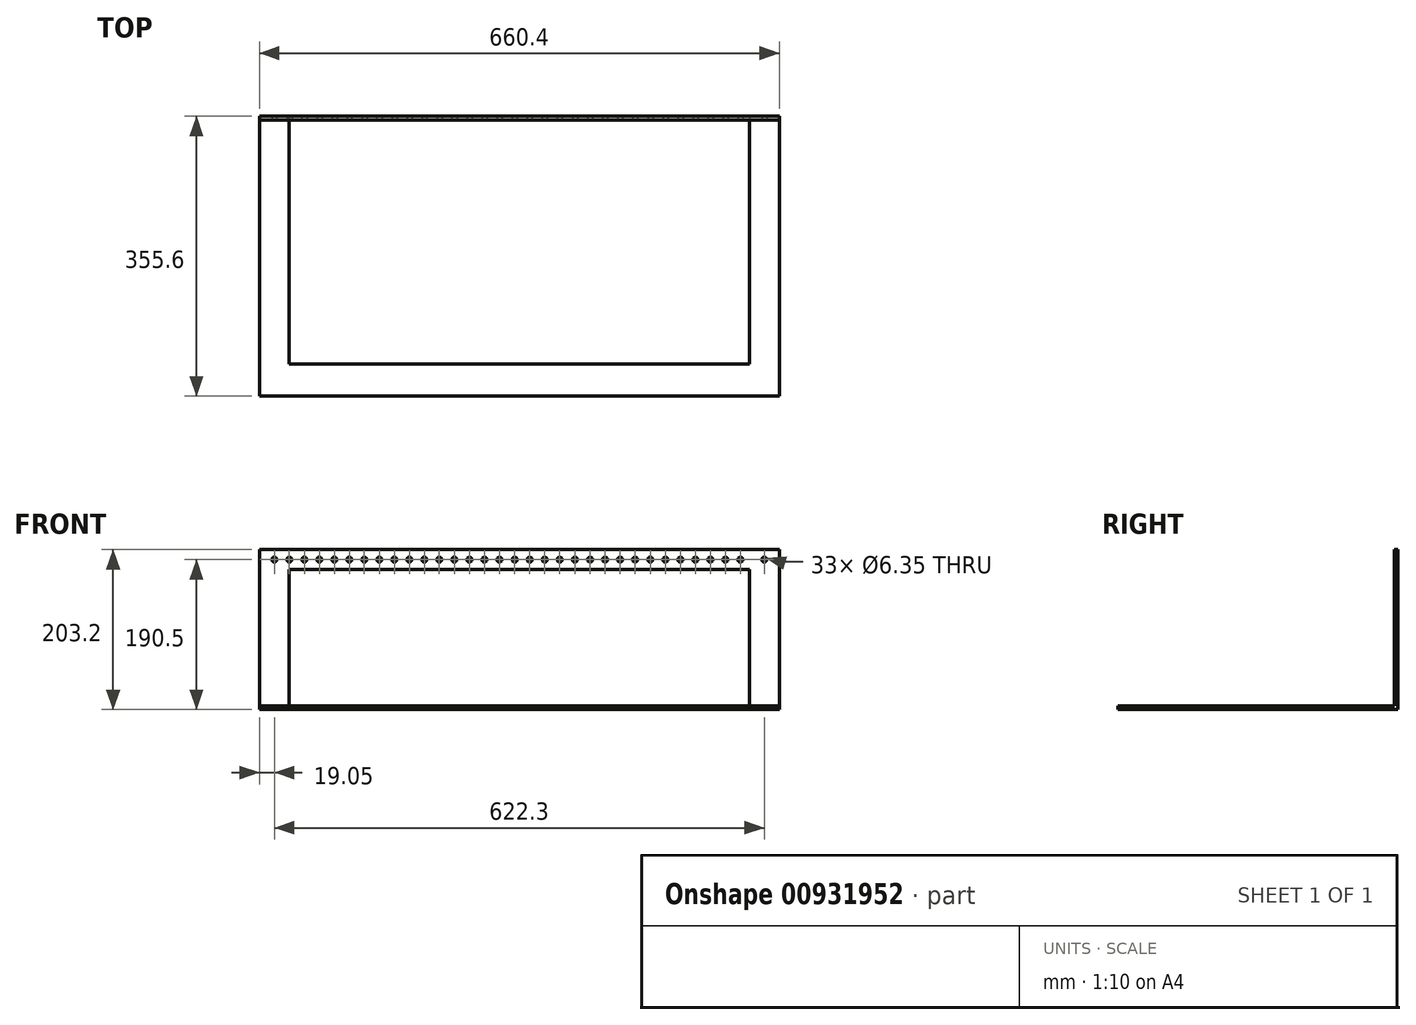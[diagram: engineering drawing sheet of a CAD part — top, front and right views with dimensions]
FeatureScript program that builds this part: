
annotation { "Feature Type Name" : "Feature", "Feature Type Description" : "" }
export const myFeature = defineFeature(function(context is Context, id is Id, definition is map)
    precondition{}
    {
        {
            var Q0;
            Q0=qCreatedBy(makeId("Right.planeOp"),FACE);
            var sketch = newSketch(context, id + "F0", { "sketchPlane" : qUnion([Q0])});
            skLineSegment(sketch, "E0", {"start": v(-188.84, 0) * mm, "end": v(166.76, 0) * mm});
            skLineSegment(sketch, "E1", {"start": v(166.76, 0) * mm, "end": v(166.76, 203.2) * mm});
            skLineSegment(sketch, "E2", {"start": v(-188.84, 0) * mm, "end": v(-188.84, 4.78) * mm});
            skLineSegment(sketch, "E3", {"start": v(-188.84, 4.78) * mm, "end": v(161.98, 4.78) * mm});
            skLineSegment(sketch, "E4", {"start": v(161.98, 4.78) * mm, "end": v(161.98, 203.2) * mm});
            skLineSegment(sketch, "E5", {"start": v(161.98, 203.2) * mm, "end": v(166.76, 203.2) * mm});
            skSolve(sketch);
        }
        {
            var Q0;
            Q0=makeQuery(id+"F0.imprint","IMPRINT",FACE,{"disambiguationData":[TD([[makeQuery(id+"F0.imprint","IMPRINT",EDGE,{"derivedFrom":sQuery(id+"F0.wireOp",EDGE,"E0")}),1.0]])]});
            extrude(context, id + "F1", {"entities" : qUnion([Q0]), "depth" : 660.4 * mm, "offsetDistance" : 25.4 * mm});
        }
        {
            var Q0;
            Q0=makeQuery(id+"F1.opExtrude","SWEPT_FACE",FACE,{"disambiguationData":[OSD([sQuery(id+"F0.wireOp",EDGE,"E2")])]});
            var sketch = newSketch(context, id + "F2", { "sketchPlane" : qUnion([Q0])});
            skLineSegment(sketch, "E6", {"start": v(38.1, 4.78) * mm, "end": v(38.1, 177.8) * mm});
            skLineSegment(sketch, "E7", {"start": v(38.1, 177.8) * mm, "end": v(622.3, 177.8) * mm});
            skLineSegment(sketch, "E8", {"start": v(622.3, 177.8) * mm, "end": v(622.3, 4.78) * mm});
            skLineSegment(sketch, "E9", {"start": v(622.3, 4.78) * mm, "end": v(38.1, 4.78) * mm});
            skSolve(sketch);
        }
        {
            var Q0;
            Q0=makeQuery(id+"F2.imprint","IMPRINT",FACE,{"disambiguationData":[TD([[makeQuery(id+"F2.imprint","IMPRINT",EDGE,{"derivedFrom":sQuery(id+"F2.wireOp",EDGE,"E6")}),-1.0]])]});
            extrude(context, id + "F3", {"entities" : qUnion([Q0]), "operationType" : NewBodyOperationType.REMOVE, "endBound" : BoundingType.THROUGH_ALL, "oppositeDirection" : true, "depth" : 254 * mm, "offsetDistance" : 25.4 * mm});
        }
        {
            var Q0;
            Q0=makeQuery(id+"F3.boolean.opBoolean","MERGE",FACE,{"derivedFrom":[makeQuery(id+"F1.opExtrude","SWEPT_FACE",FACE,{"disambiguationData":[OSD([sQuery(id+"F0.wireOp",EDGE,"E3")])]})],"fromTools":[makeQuery(id+"F3.opExtrude","SWEPT_FACE",FACE,{"disambiguationData":[OSD([sQuery(id+"F2.wireOp",EDGE,"E9")])]})]});
            var sketch = newSketch(context, id + "F4", { "sketchPlane" : qUnion([Q0])});
            skLineSegment(sketch, "E10", {"start": v(38.1, 166.76) * mm, "end": v(38.1, -148.16) * mm});
            skLineSegment(sketch, "E11", {"start": v(38.1, -148.16) * mm, "end": v(622.3, -148.16) * mm});
            skLineSegment(sketch, "E12", {"start": v(622.3, -148.16) * mm, "end": v(622.3, 166.76) * mm});
            skLineSegment(sketch, "E13", {"start": v(622.3, 166.76) * mm, "end": v(38.1, 166.76) * mm});
            skLineSegment(sketch, "E14", {"start": v(38.1, 161.98) * mm, "end": v(38.1, 166.76) * mm});
            skSolve(sketch);
        }
        {
            var Q0;
            Q0 = qSketchRegion(id + "F4", true);
            extrude(context, id + "F5", {"entities" : qUnion([Q0]), "operationType" : NewBodyOperationType.REMOVE, "oppositeDirection" : true, "depth" : 25.4 * mm, "offsetDistance" : 25.4 * mm});
        }
        {
            var Q0;
            Q0=makeQuery(id+"F1.opExtrude","SWEPT_FACE",FACE,{"disambiguationData":[OSD([sQuery(id+"F0.wireOp",EDGE,"E4")])]});
            var sketch = newSketch(context, id + "F6", { "sketchPlane" : qUnion([Q0])});
            skLineSegment(sketch, "E15", {"start": v(0, 190.5) * mm, "end": v(114.3, 190.5) * mm, "construction": true});
            skLineSegment(sketch, "E16", {"start": v(114.3, 190.5) * mm, "end": v(660.4, 190.5) * mm, "construction": true});
            skPoint(sketch, "E17", {"position": v(19.05, 190.5) * mm});
            skPoint(sketch, "E18", {"position": v(38.1, 190.5) * mm});
            skPoint(sketch, "E19", {"position": v(57.15, 190.5) * mm});
            skPoint(sketch, "E20", {"position": v(76.2, 190.5) * mm});
            skPoint(sketch, "E21", {"position": v(95.25, 190.5) * mm});
            skPoint(sketch, "E22", {"position": v(114.3, 190.5) * mm});
            skPoint(sketch, "E23", {"position": v(133.35, 190.5) * mm});
            skPoint(sketch, "E24", {"position": v(152.4, 190.5) * mm});
            skPoint(sketch, "E25", {"position": v(171.45, 190.5) * mm});
            skPoint(sketch, "E26", {"position": v(190.5, 190.5) * mm});
            skPoint(sketch, "E27", {"position": v(209.55, 190.5) * mm});
            skPoint(sketch, "E28", {"position": v(228.6, 190.5) * mm});
            skPoint(sketch, "E29", {"position": v(247.65, 190.5) * mm});
            skPoint(sketch, "E30.1.0.0", {"position": v(305.05, 190.5) * mm});
            skPoint(sketch, "E30.1.0.1", {"position": v(286, 190.5) * mm});
            skPoint(sketch, "E30.1.0.2", {"position": v(266.95, 190.5) * mm});
            skPoint(sketch, "E30.1.0.3", {"position": v(247.9, 190.5) * mm});
            skLineSegment(sketch, "E30.1.0.4", {"start": v(190.75, 190.5) * mm, "end": v(736.85, 190.5) * mm, "construction": true});
            skPoint(sketch, "E30.2.0.0", {"position": v(381.5, 190.5) * mm});
            skPoint(sketch, "E30.2.0.1", {"position": v(362.46, 190.5) * mm});
            skPoint(sketch, "E30.2.0.2", {"position": v(343.4, 190.5) * mm});
            skPoint(sketch, "E30.2.0.3", {"position": v(324.36, 190.5) * mm});
            skLineSegment(sketch, "E30.2.0.4", {"start": v(267.2, 190.5) * mm, "end": v(813.3, 190.5) * mm, "construction": true});
            skLineSegment(sketch, "E30.direction1", {"start": v(228.6, 190.5) * mm, "end": v(305.05, 190.5) * mm, "construction": true});
            skPoint(sketch, "E31.1.0.0", {"position": v(381.76, 190.5) * mm});
            skPoint(sketch, "E31.1.0.1", {"position": v(477.27, 190.5) * mm});
            skPoint(sketch, "E31.1.0.2", {"position": v(458.22, 190.5) * mm});
            skPoint(sketch, "E31.1.0.3", {"position": v(439.17, 190.5) * mm});
            skPoint(sketch, "E31.1.0.4", {"position": v(420.12, 190.5) * mm});
            skPoint(sketch, "E31.1.0.5", {"position": v(400.81, 190.5) * mm});
            skPoint(sketch, "E31.2.0.0", {"position": v(477.52, 190.5) * mm});
            skPoint(sketch, "E31.2.0.1", {"position": v(573.02, 190.5) * mm});
            skPoint(sketch, "E31.2.0.2", {"position": v(553.97, 190.5) * mm});
            skPoint(sketch, "E31.2.0.3", {"position": v(534.92, 190.5) * mm});
            skPoint(sketch, "E31.2.0.4", {"position": v(515.87, 190.5) * mm});
            skPoint(sketch, "E31.2.0.5", {"position": v(496.57, 190.5) * mm});
            skLineSegment(sketch, "E31.direction1", {"start": v(286, 190.5) * mm, "end": v(381.76, 190.5) * mm, "construction": true});
            skPoint(sketch, "E32", {"position": v(641.35, 190.5) * mm});
            skPoint(sketch, "E33", {"position": v(611.12, 190.5) * mm});
            skPoint(sketch, "E34", {"position": v(592.07, 190.5) * mm});
            skSolve(sketch);
        }
        {
            var Q0;
            Q0=sQuery(id+"F6.wireOp",VERTEX,"E17");
            var Q1;
            Q1=sQuery(id+"F6.wireOp",VERTEX,"E18");
            var Q2;
            Q2=sQuery(id+"F6.wireOp",VERTEX,"E19");
            var Q3;
            Q3=sQuery(id+"F6.wireOp",VERTEX,"E20");
            var Q4;
            Q4=sQuery(id+"F6.wireOp",VERTEX,"E21");
            var Q5;
            Q5=sQuery(id+"F6.wireOp",VERTEX,"E22");
            var Q6;
            Q6=sQuery(id+"F6.wireOp",VERTEX,"E23");
            var Q7;
            Q7=sQuery(id+"F6.wireOp",VERTEX,"E24");
            var Q8;
            Q8=sQuery(id+"F6.wireOp",VERTEX,"E25");
            var Q9;
            Q9=sQuery(id+"F6.wireOp",VERTEX,"E26");
            var Q10;
            Q10=sQuery(id+"F6.wireOp",VERTEX,"E27");
            var Q11;
            Q11=sQuery(id+"F6.wireOp",VERTEX,"E28");
            var Q12;
            Q12=sQuery(id+"F6.wireOp",VERTEX,"E29");
            var Q13;
            Q13=sQuery(id+"F6.wireOp",VERTEX,"E30.1.0.2");
            var Q14;
            Q14=sQuery(id+"F6.wireOp",VERTEX,"E30.1.0.1");
            var Q15;
            Q15=sQuery(id+"F6.wireOp",VERTEX,"E30.1.0.0");
            var Q16;
            Q16=sQuery(id+"F6.wireOp",VERTEX,"E30.2.0.3");
            var Q17;
            Q17=sQuery(id+"F6.wireOp",VERTEX,"E30.2.0.2");
            var Q18;
            Q18=sQuery(id+"F6.wireOp",VERTEX,"E30.2.0.1");
            var Q19;
            Q19=sQuery(id+"F6.wireOp",VERTEX,"E30.2.0.0");
            var Q20;
            Q20=sQuery(id+"F6.wireOp",VERTEX,"E31.1.0.5");
            var Q21;
            Q21=sQuery(id+"F6.wireOp",VERTEX,"E31.1.0.4");
            var Q22;
            Q22=sQuery(id+"F6.wireOp",VERTEX,"E31.1.0.3");
            var Q23;
            Q23=sQuery(id+"F6.wireOp",VERTEX,"E31.1.0.2");
            var Q24;
            Q24=sQuery(id+"F6.wireOp",VERTEX,"E31.1.0.1");
            var Q25;
            Q25=sQuery(id+"F6.wireOp",VERTEX,"E31.2.0.5");
            var Q26;
            Q26=sQuery(id+"F6.wireOp",VERTEX,"E31.2.0.4");
            var Q27;
            Q27=sQuery(id+"F6.wireOp",VERTEX,"E31.2.0.3");
            var Q28;
            Q28=sQuery(id+"F6.wireOp",VERTEX,"E31.2.0.2");
            var Q29;
            Q29=sQuery(id+"F6.wireOp",VERTEX,"E31.2.0.1");
            var Q30;
            Q30=sQuery(id+"F6.wireOp",VERTEX,"E33");
            var Q31;
            Q31=sQuery(id+"F6.wireOp",VERTEX,"E34");
            var Q32;
            Q32=sQuery(id+"F6.wireOp",VERTEX,"E32");
            var Q33;
            Q33=makeQuery(id+"F1.opExtrude","SWEPT_BODY",BODY,{"disambiguationData":[OSD([sQuery(id+"F0.wireOp",EDGE,"E0"),sQuery(id+"F0.wireOp",EDGE,"E1"),sQuery(id+"F0.wireOp",EDGE,"E2"),sQuery(id+"F0.wireOp",EDGE,"E3"),sQuery(id+"F0.wireOp",EDGE,"E4"),sQuery(id+"F0.wireOp",EDGE,"E5")])]});
            hole(context, id + "F7", {"style" : HoleStyle.SIMPLE, "endStyle" : HoleEndStyle.THROUGH, "holeDiameter" : 6.35 * mm, "majorDiameter" : 6.35 * mm, "tappedDepth" : 48.26 * mm, "tapClearance" : 3, "startFromSketch" : true, "locations" : qUnion([Q0, Q1, Q2, Q3, Q4, Q5, Q6, Q7, Q8, Q9, Q10, Q11, Q12, Q13, Q14, Q15, Q16, Q17, Q18, Q19, Q20, Q21, Q22, Q23, Q24, Q25, Q26, Q27, Q28, Q29, Q30, Q31, Q32]), "scope" : qUnion([Q33])});
        }
    });
